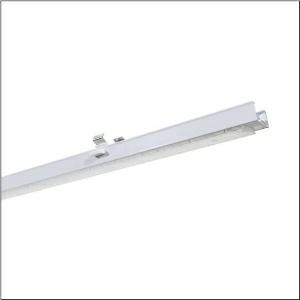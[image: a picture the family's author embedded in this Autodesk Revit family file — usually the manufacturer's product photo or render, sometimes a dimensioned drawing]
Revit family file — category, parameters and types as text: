
# Revit family: sanierungs-leuchteneinsatz_31_gen_2_51re12mb5cb_f4e6
name_source: partatom
category: Lighting Fixtures
units: mm (PartAtom-declared; Revit-internal decimal feet)

## family parameters
Cut with Voids When Loaded = No
Host = Face
Light Source = No
Part Type = Normal
Room Calculation Point = No
Round Connector Dimension = Use Diameter
Shared = No

## types (1)
- --- (1 x LED, 11500 lm, 66 W, 5000K)
    Apparent Load = 66 VA
    CIE Flux Codes = 65 91 98 99 100
    Color Rendering = 80
    Color Temperature = 5000K
    Default Elevation = 1800 mm
    Description = Refurbishment luminaire insert Gen.2, luminaire insert, of extruded aluminium section, coated, traffic white (RAL 9016), length: 1.472mm, width: 91mm, height: 53mm, LED rated luminous flux: 11.500lm, light colour: 850, control gear: ON/OFF Multilumen, with system connector: socket, mains connection: 220..240V, AC, 50/60Hz, luminous flux adjustable on luminaire in eight steps (3450/4380/5800/6700/8350/9200/10500/11500lm ), connected load according to luminous flux setting (19/24/32/37/47/52/60/66W), primary light control with lens, of plastic, primary optical cover: cover, of PMMA, light emission: direct distribution, protection rating (complete): IP20, insulation class (complete): insulation class I (protective earthing), certification: CE, UKCA, impact resistance: IK02, permissible ambient temperature for indoor applications: -20..+40°C, packaging unit: 1 piece
    Height = 58 mm
    Lamp = 1 x LED
    Lamp Light Flux = 11500 lm
    Lamp Power = 66 W
    Lamp count = 1
    Length = 1472 mm
    Luminous efficacy = 174 lm/W
    Manufacturer = Siteco
    ModVariant = No
    Model = 51RE12MB5CB
    Mounting Place = Ceiling
    Mounting Type = Pendant
    Number of Poles = 1
    OnlyDefault = Yes
    Power Factor = 1
    Product Name = Sanierungs-Leuchteneinsatz 31 Gen.2
    Product group = luminaire insert
    ProductGroupID = 902
    Protection Class = Protection class I
    Protection Degree = IP 20
    RLX_Detail_Level = 1
    RlxData = <blob elided: 21065 chars, md5=913ab5ef>
    Socket = socket
    Standby Power = 0 W
    System Light Flux = 11500 lm
    System Power = 66 W
    Type Comments = factory setting: luminous flux: 100 % | (ON | ON | ON)
    Type Image = l_1266702.jpg
    URL = http://relux.com
    VarID = @adj_049511
    Voltage = 0 V
    Weight = 0.00 kg
    Width = 65 mm

## geometry (parser evidence)
native form markers: Blend x4, Sweep x10
no freeform markers — native parametric forms only
